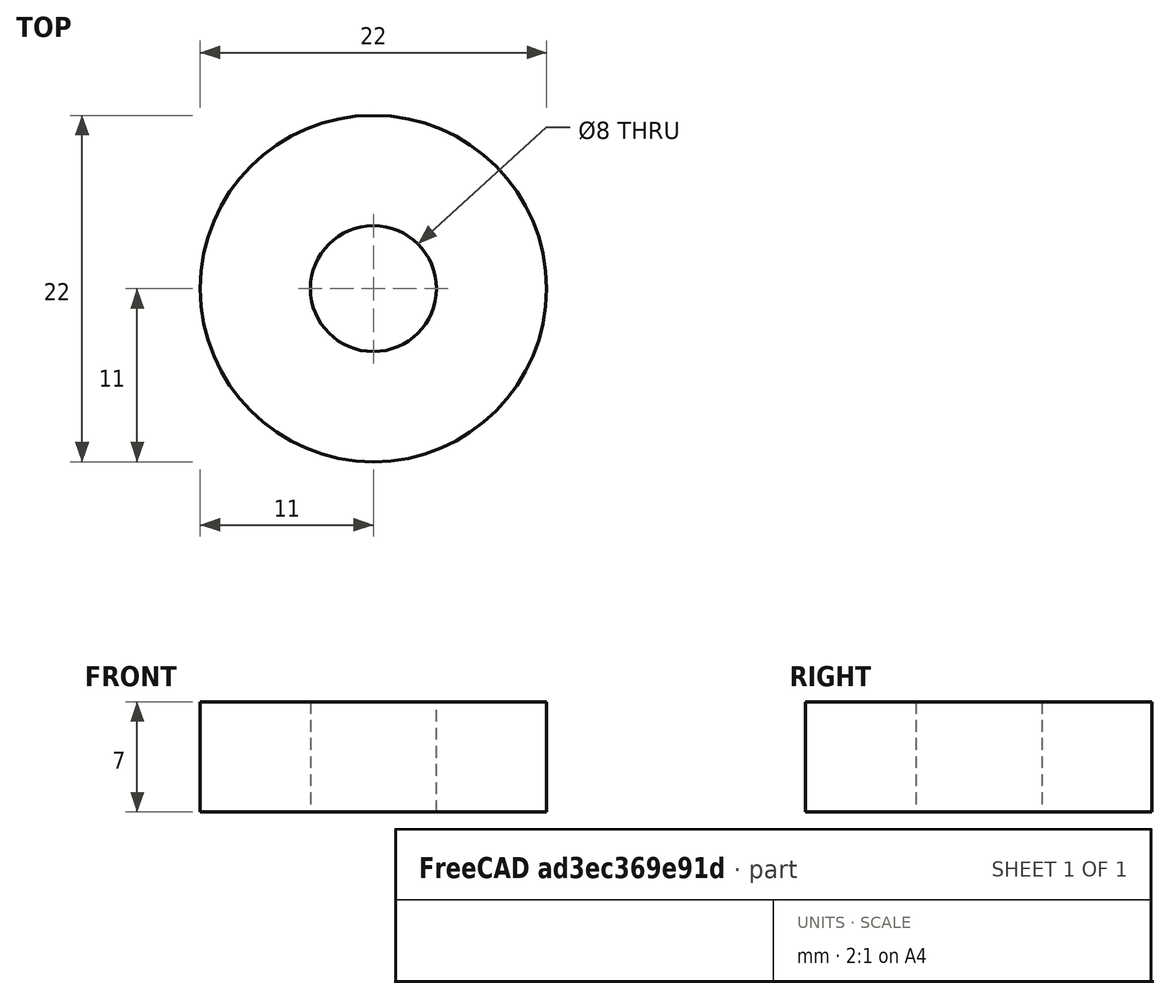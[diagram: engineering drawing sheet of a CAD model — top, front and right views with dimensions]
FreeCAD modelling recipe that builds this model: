
FCSTD DOCUMENT  (FreeCAD 1.0R39109 (Git))
Label: Подшипник 608
License: All rights reserved
LicenseURL: https://en.wikipedia.org/wiki/All_rights_reserved
objects: Sketcher::SketchObject×1, PartDesign::Pad×1, PartDesign::Body×1
note: 6 computed .brp shape members not serialized (recipe doc carries the construction recipe); baked Part::Feature solids carry a one-line shape summary decoded from their .brp

FEATURE [Sketcher::SketchObject] Sketch
  ArcFitTolerance = 1e-06
  AttachmentSupport = -> [XY_Plane]
  FullyConstrained = true
  MakeInternals = false
  MapMode = 5
  sketch-geometry (2):
    g0: Circle CenterX=0 CenterY=0 CenterZ=0 NormalX=0 NormalY=0 NormalZ=1 AngleXU=0 Radius=11
    g1: Circle CenterX=0 CenterY=0 CenterZ=0 NormalX=0 NormalY=0 NormalZ=1 AngleXU=0 Radius=4
  constraints (4):
    c: Diameter(g0) = 22
    c: Coincident(g0,g-1)
    c: Diameter(g1) = 8
    c: Coincident(g1,g0)
FEATURE [PartDesign::Pad] Pad
  Direction = (0,0,1)
  Length = 7
  Length2 = 10
  Profile = -> Sketch
  ReferenceAxis = -> Sketch [N_Axis]
  Refine = true
  Suppressed = false
  Type = 0
FEATURE [PartDesign::Body] Body  label="Тело"
  AllowCompound = false
  Group = -> [Sketch,Pad]
  Origin = -> Origin
  Tip = -> Pad
